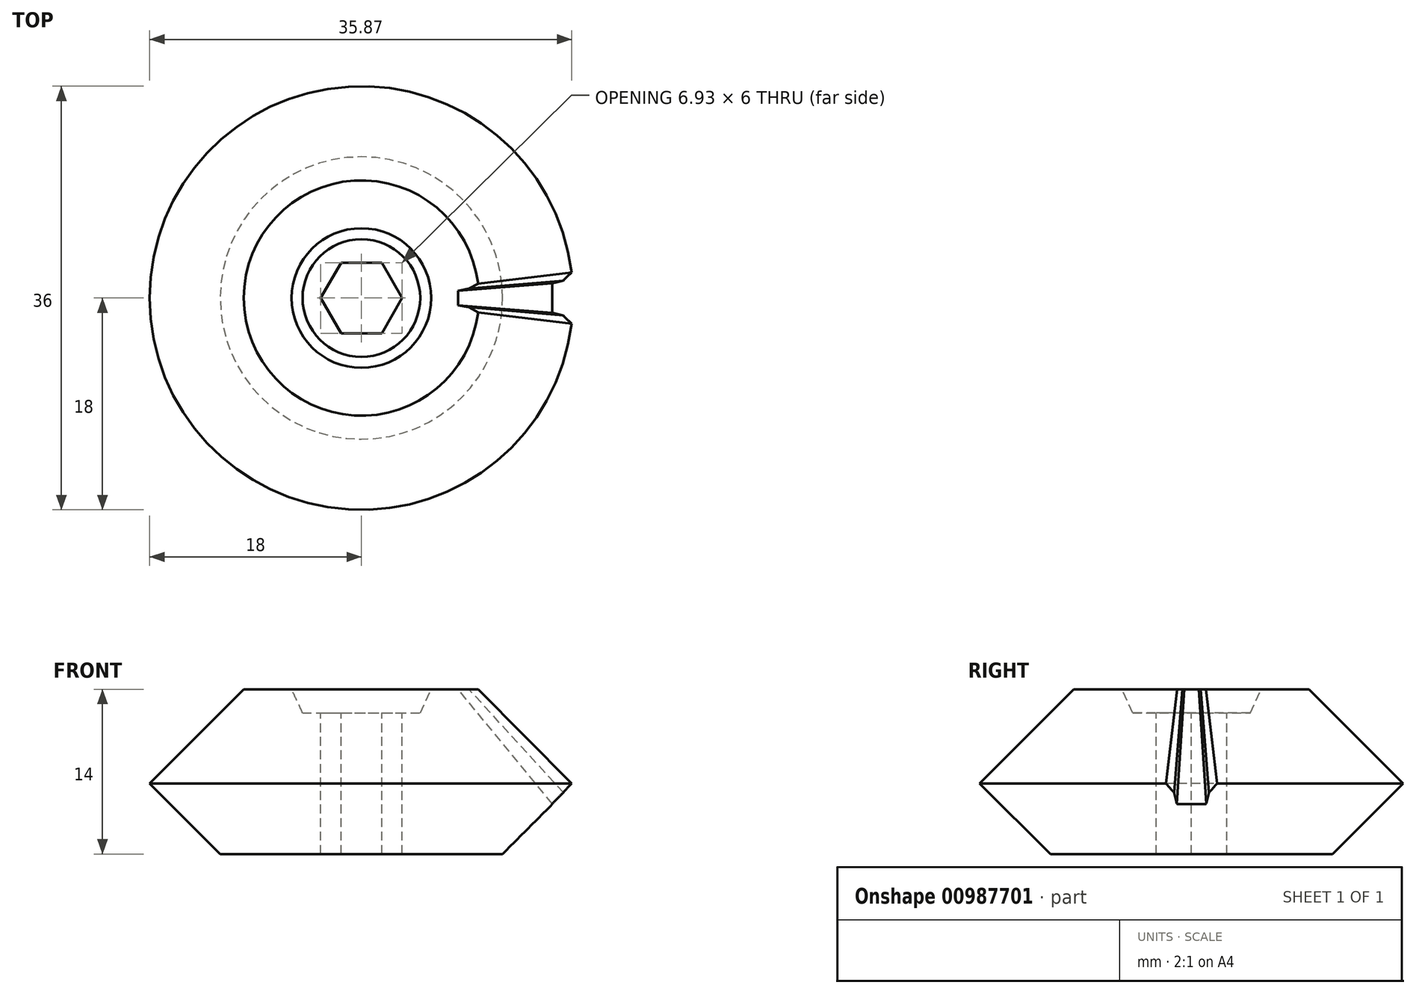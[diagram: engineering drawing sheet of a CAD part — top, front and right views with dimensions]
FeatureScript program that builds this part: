
annotation { "Feature Type Name" : "Feature", "Feature Type Description" : "" }
export const myFeature = defineFeature(function(context is Context, id is Id, definition is map)
    precondition{}
    {
        {
            var Q0;
            Q0=qCreatedBy(makeId("Front.planeOp"),FACE);
            var sketch = newSketch(context, id + "F0", { "sketchPlane" : qUnion([Q0])});
            skLineSegment(sketch, "E0", {"start": v(18, 6) * mm, "end": v(0, 24) * mm});
            skLineSegment(sketch, "E1", {"start": v(0, 24) * mm, "end": v(0, 0) * mm});
            skLineSegment(sketch, "E2", {"start": v(0, 0) * mm, "end": v(12, 0) * mm});
            skLineSegment(sketch, "E3", {"start": v(12, 0) * mm, "end": v(18, 6) * mm});
            skSolve(sketch);
        }
        {
            var Q0;
            Q0=makeQuery(id+"F0.imprint","IMPRINT",FACE,{"disambiguationData":[TD([[makeQuery(id+"F0.imprint","IMPRINT",EDGE,{"derivedFrom":sQuery(id+"F0.wireOp",EDGE,"iZfwdum0-eERQ-opZv-YKFB-7AKXDabp0p0H")}),1.0]])]});
            var Q1;
            Q1=makeQuery(id+"F0.imprint","IMPRINT",FACE,{"disambiguationData":[TD([[makeQuery(id+"F0.imprint","IMPRINT",EDGE,{"derivedFrom":sQuery(id+"F0.wireOp",EDGE,"E0")}),1.0]])]});
            var Q2;
            Q2=sQuery(id+"F0.wireOp",EDGE,"E1");
            revolve(context, id + "F1", {"surfaceOperationType" : NewSurfaceOperationType.NEW, "entities" : qUnion([Q0, Q1]), "axis" : qUnion([Q2]), "revolveType" : RevolveType.FULL});
        }
        {
            var Q0;
            Q0=sQuery(id+"F0.wireOp",EDGE,"E0");
            var Q1;
            Q1=sQuery(id+"F0.wireOp",VERTEX,"E0.start");
            cPlane(context, id + "F2", {"entities" : qUnion([Q0, Q1]), "cplaneType" : CPlaneType.LINE_POINT, "offset" : 25 * mm, "width" : 150 * mm, "height" : 150 * mm});
        }
        {
            var Q0;
            Q0=qCreatedBy(id+"F2.planeOp",FACE);
            var sketch = newSketch(context, id + "F3", { "sketchPlane" : qUnion([Q0])});
            skPoint(sketch, "E4.0", {"position": v(0, 16.97) * mm});
            skLineSegment(sketch, "E5", {"start": v(0, 0) * mm, "end": v(-4.6, 29.03) * mm, "construction": true});
            skLineSegment(sketch, "E6", {"start": v(0, 0) * mm, "end": v(0, 16.97) * mm, "construction": true});
            skLineSegment(sketch, "E7", {"start": v(0, 14.47) * mm, "end": v(-1.25, 14.47) * mm});
            skLineSegment(sketch, "E8", {"start": v(-1.25, 14.47) * mm, "end": v(-1.49, 15.83) * mm});
            skLineSegment(sketch, "E9", {"start": v(-1.49, 15.83) * mm, "end": v(-2.25, 16.97) * mm});
            skLineSegment(sketch, "E10", {"start": v(-1.25, 14.47) * mm, "end": v(-2.25, 16.97) * mm, "construction": true});
            skLineSegment(sketch, "E11", {"start": v(-1.49, 15.83) * mm, "end": v(-1.75, 15.72) * mm, "construction": true});
            skLineSegment(sketch, "E12.MirrorCS", {"start": v(0, 14.47) * mm, "end": v(1.25, 14.47) * mm});
            skLineSegment(sketch, "E13.MirrorCS", {"start": v(1.25, 14.47) * mm, "end": v(1.49, 15.83) * mm});
            skLineSegment(sketch, "E14.MirrorCS", {"start": v(1.49, 15.83) * mm, "end": v(2.25, 16.97) * mm});
            skLineSegment(sketch, "E15", {"start": v(2.25, 16.97) * mm, "end": v(-2.25, 16.97) * mm});
            skSolve(sketch);
        }
        {
            var Q0;
            Q0=makeQuery(id+"F3.imprint","IMPRINT",FACE,{"disambiguationData":[TD([[makeQuery(id+"F3.imprint","IMPRINT",EDGE,{"derivedFrom":sQuery(id+"F3.wireOp",EDGE,"E7")}),-1.0]])]});
            var Q1;
            Q1=makeQuery(id+"F1.opRevolve","SWEPT_VERTEX",VERTEX,{"disambiguationData":[OSD([sQuery(id+"F0.wireOp",EDGE,"E0"),sQuery(id+"F0.wireOp",EDGE,"E1")])]});
            loft(context, id + "F4", {"operationType" : NewBodyOperationType.REMOVE, "sheetProfilesArray" : [{ "sheetProfileEntities" : qUnion([Q0]) }, { "sheetProfileEntities" : qUnion([Q1]) }]});
        }
        {
            var Q0;
            Q0=qCreatedBy(makeId("Front.planeOp"),FACE);
            var sketch = newSketch(context, id + "F5", { "sketchPlane" : qUnion([Q0])});
            skPoint(sketch, "E16.0", {"position": v(0, 24) * mm});
            skLineSegment(sketch, "E17", {"start": v(0, 24) * mm, "end": v(0, 12) * mm});
            skLineSegment(sketch, "E18", {"start": v(0, 12) * mm, "end": v(5, 12) * mm});
            skLineSegment(sketch, "E19", {"start": v(5, 12) * mm, "end": v(5.93, 14) * mm});
            skLineSegment(sketch, "E20", {"start": v(5.93, 14) * mm, "end": v(21.55, 14) * mm});
            skLineSegment(sketch, "E21", {"start": v(21.55, 14) * mm, "end": v(0, 24) * mm});
            skSolve(sketch);
        }
        {
            var Q0;
            Q0=makeQuery(id+"F5.imprint","IMPRINT",FACE,{"disambiguationData":[TD([[makeQuery(id+"F5.imprint","IMPRINT",EDGE,{"derivedFrom":sQuery(id+"F5.wireOp",EDGE,"E17")}),1.0]])]});
            var Q1;
            Q1=sQuery(id+"F5.wireOp",EDGE,"E17");
            revolve(context, id + "F6", {"operationType" : NewBodyOperationType.REMOVE, "surfaceOperationType" : NewSurfaceOperationType.NEW, "entities" : qUnion([Q0]), "axis" : qUnion([Q1]), "revolveType" : RevolveType.FULL, "oppositeDirection" : true});
        }
        {
            var Q0;
            Q0=makeQuery(id+"F6.boolean.opBoolean","COPY",FACE,{"derivedFrom":makeQuery(id+"F6.opRevolve","SWEPT_FACE",FACE,{"disambiguationData":[OSD([sQuery(id+"F5.wireOp",EDGE,"E18")])]})});
            var sketch = newSketch(context, id + "F7", { "sketchPlane" : qUnion([Q0])});
            skCircle(sketch, "E22.cCircle", {"center": v(0, 0) * mm, "radius": 3 * mm, "construction": true});
            skLineSegment(sketch, "E22.0", {"start": v(-1.73, 3) * mm, "end": v(1.73, 3) * mm});
            skLineSegment(sketch, "E22.1", {"start": v(1.73, 3) * mm, "end": v(3.46, 0) * mm});
            skLineSegment(sketch, "E22.2", {"start": v(3.46, 0) * mm, "end": v(1.73, -3) * mm});
            skLineSegment(sketch, "E22.3", {"start": v(1.73, -3) * mm, "end": v(-1.73, -3) * mm});
            skLineSegment(sketch, "E22.4", {"start": v(-1.73, -3) * mm, "end": v(-3.46, 0) * mm});
            skLineSegment(sketch, "E22.5", {"start": v(-3.46, 0) * mm, "end": v(-1.73, 3) * mm});
            skPoint(sketch, "E22.0.midPoint", {"position": v(0, 3) * mm});
            skSolve(sketch);
        }
        {
            var Q0;
            Q0=makeQuery(id+"F7.imprint","IMPRINT",FACE,{"disambiguationData":[TD([[makeQuery(id+"F7.imprint","IMPRINT",EDGE,{"derivedFrom":sQuery(id+"F7.wireOp",EDGE,"E22.0")}),-1.0]])]});
            extrude(context, id + "F8", {"entities" : qUnion([Q0]), "operationType" : NewBodyOperationType.REMOVE, "endBound" : BoundingType.THROUGH_ALL, "oppositeDirection" : true, "depth" : 25 * mm, "offsetDistance" : 25 * mm});
        }
    });
